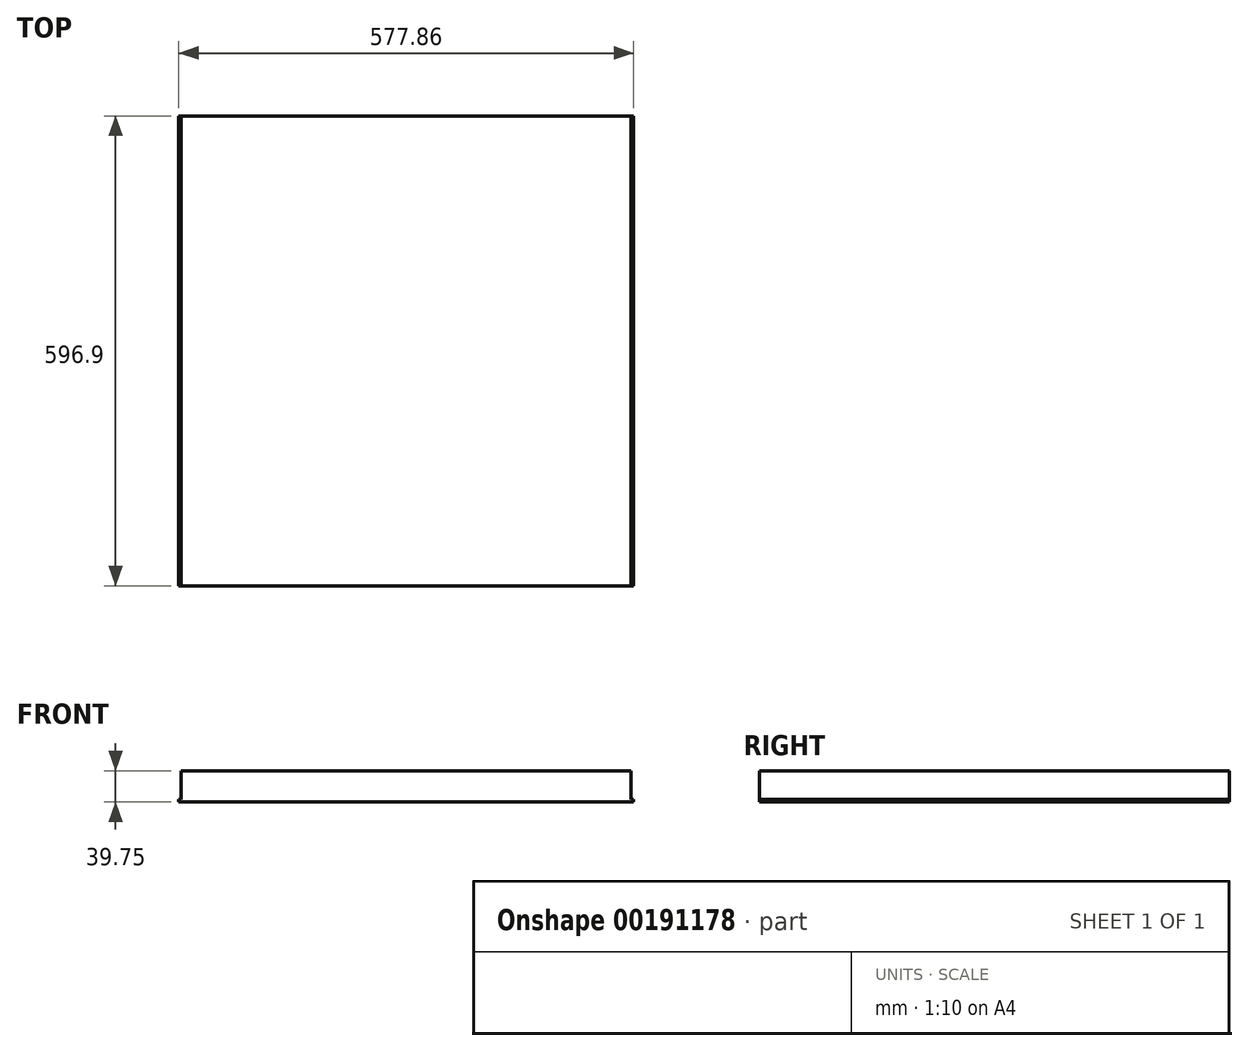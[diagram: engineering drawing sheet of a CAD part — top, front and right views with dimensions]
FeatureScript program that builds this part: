
annotation { "Feature Type Name" : "Feature", "Feature Type Description" : "" }
export const myFeature = defineFeature(function(context is Context, id is Id, definition is map)
    precondition{}
    {
        {
            var Q0;
            Q0=qCreatedBy(makeId("Top.planeOp"),FACE);
            var sketch = newSketch(context, id + "F0", { "sketchPlane" : qUnion([Q0])});
            skLineSegment(sketch, "E0.bottom", {"start": v(285.75, -298.45) * mm, "end": v(-285.75, -298.45) * mm});
            skLineSegment(sketch, "E0.top", {"start": v(285.75, 298.45) * mm, "end": v(-285.75, 298.45) * mm});
            skLineSegment(sketch, "E0.left", {"start": v(285.75, -298.45) * mm, "end": v(285.75, 298.45) * mm});
            skLineSegment(sketch, "E0.right", {"start": v(-285.75, -298.45) * mm, "end": v(-285.75, 298.45) * mm});
            skPoint(sketch, "E0.middle", {"position": v(0, 0) * mm});
            skSolve(sketch);
        }
        {
            var Q0;
            Q0=qSketchRegion(id+"F0",true);
            extrude(context, id + "F1", {"entities" : qUnion([Q0]), "depth" : 36.58 * mm});
        }
        {
            var Q0;
            Q0=makeQuery(id+"F1.opExtrude","CAP_FACE",FACE,{"disambiguationData":[OSD([sQuery(id+"F0.wireOp",EDGE,"E0.bottom"),sQuery(id+"F0.wireOp",EDGE,"E0.top"),sQuery(id+"F0.wireOp",EDGE,"E0.left"),sQuery(id+"F0.wireOp",EDGE,"E0.right")])],"isStart":true});
            var sketch = newSketch(context, id + "F2", { "sketchPlane" : qUnion([Q0])});
            skLineSegment(sketch, "E1.bottom", {"start": v(288.93, 298.45) * mm, "end": v(-288.92, 298.45) * mm});
            skLineSegment(sketch, "E1.top", {"start": v(288.92, -298.45) * mm, "end": v(-288.93, -298.45) * mm});
            skLineSegment(sketch, "E1.left", {"start": v(288.93, 298.45) * mm, "end": v(288.92, -298.45) * mm});
            skLineSegment(sketch, "E1.right", {"start": v(-288.92, 298.45) * mm, "end": v(-288.93, -298.45) * mm});
            skPoint(sketch, "E1.middle", {"position": v(0, 0) * mm});
            skSolve(sketch);
        }
        {
            var Q0;
            Q0=qSketchRegion(id+"F2",true);
            extrude(context, id + "F3", {"entities" : qUnion([Q0]), "operationType" : NewBodyOperationType.ADD, "depth" : 3.17 * mm});
        }
    });
